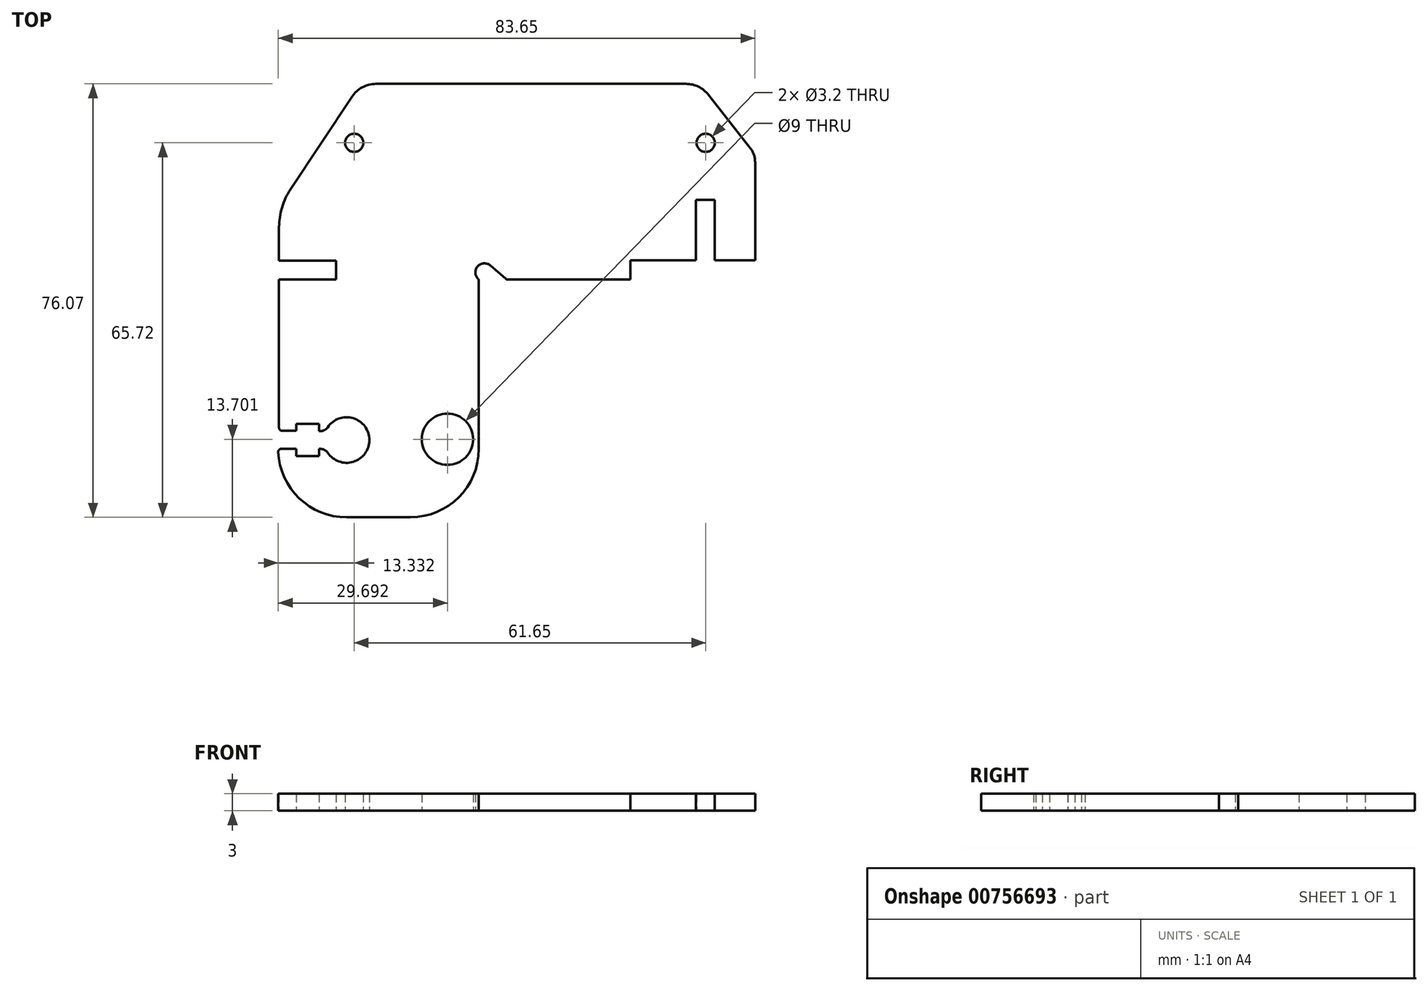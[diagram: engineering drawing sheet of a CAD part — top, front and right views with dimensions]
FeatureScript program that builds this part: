
annotation { "Feature Type Name" : "Feature", "Feature Type Description" : "" }
export const myFeature = defineFeature(function(context is Context, id is Id, definition is map)
    precondition{}
    {
        {
            var Q0;
            Q0=qCreatedBy(makeId("Top.planeOp"),FACE);
            var sketch = newSketch(context, id + "F0", { "sketchPlane" : qUnion([Q0])});
            skLineSegment(sketch, "E0", {"start": v(29.23, 6.23) * mm, "end": v(29.23, 14.01) * mm});
            skLineSegment(sketch, "E1", {"start": v(32.53, 14.01) * mm, "end": v(29.23, 14.01) * mm});
            skLineSegment(sketch, "E2", {"start": v(32.53, 14.01) * mm, "end": v(32.53, 3.36) * mm});
            skLineSegment(sketch, "E3", {"start": v(39.6, 3.36) * mm, "end": v(39.6, 22.01) * mm});
            skLineSegment(sketch, "E4", {"start": v(32.53, 3.36) * mm, "end": v(39.6, 3.36) * mm});
            skLineSegment(sketch, "E5", {"start": v(29.92, 34.35) * mm, "end": v(39.6, 22.01) * mm});
            skLineSegment(sketch, "E6", {"start": v(29.92, 34.35) * mm, "end": v(-29.62, 34.35) * mm});
            skLineSegment(sketch, "E7", {"start": v(-43.9, 12.82) * mm, "end": v(-29.62, 34.35) * mm});
            skLineSegment(sketch, "E8", {"start": v(-43.9, 12.82) * mm, "end": v(-43.9, 3.35) * mm});
            skLineSegment(sketch, "E9", {"start": v(29.23, 6.23) * mm, "end": v(29.23, 3.36) * mm});
            skLineSegment(sketch, "E10", {"start": v(29.23, 3.36) * mm, "end": v(17.7, 3.36) * mm});
            skLineSegment(sketch, "E11", {"start": v(17.7, 3.36) * mm, "end": v(17.7, 0) * mm});
            skLineSegment(sketch, "E12", {"start": v(17.7, 0) * mm, "end": v(-3.99, 0) * mm});
            skLineSegment(sketch, "E13", {"start": v(-43.9, 3.35) * mm, "end": v(-33.9, 3.35) * mm});
            skLineSegment(sketch, "E14", {"start": v(-33.9, 3.35) * mm, "end": v(-33.9, 0.05) * mm});
            skLineSegment(sketch, "E15", {"start": v(-33.9, 0.05) * mm, "end": v(-43.9, 0.05) * mm});
            skLineSegment(sketch, "E16", {"start": v(-43.9, 0.05) * mm, "end": v(-43.9, -26.52) * mm});
            skLineSegment(sketch, "E17", {"start": v(-43.9, -26.52) * mm, "end": v(-40.9, -26.52) * mm});
            skLineSegment(sketch, "E18", {"start": v(-40.9, -26.52) * mm, "end": v(-40.9, -25.32) * mm});
            skLineSegment(sketch, "E19", {"start": v(-40.9, -25.32) * mm, "end": v(-36.9, -25.32) * mm});
            skLineSegment(sketch, "E20", {"start": v(-36.9, -25.32) * mm, "end": v(-36.9, -26.59) * mm});
            skLineSegment(sketch, "E21", {"start": v(-36.9, -26.59) * mm, "end": v(-35.74, -26.59) * mm});
            skLineSegment(sketch, "E22", {"start": v(-40.9, -29.72) * mm, "end": v(-44.06, -29.72) * mm});
            skLineSegment(sketch, "E23", {"start": v(-40.9, -29.72) * mm, "end": v(-40.9, -30.99) * mm});
            skLineSegment(sketch, "E24", {"start": v(-40.9, -30.99) * mm, "end": v(-36.9, -30.99) * mm});
            skLineSegment(sketch, "E25", {"start": v(-36.9, -30.99) * mm, "end": v(-36.9, -29.72) * mm});
            skLineSegment(sketch, "E26", {"start": v(-36.9, -29.72) * mm, "end": v(-35.74, -29.72) * mm});
            skArc(sketch, "E27", {"start": v(-35.74, -29.72) * mm, "mid": v(-28.06, -28.15) * mm, "end": v(-35.74, -26.59) * mm});
            skLineSegment(sketch, "E28", {"start": v(-44.06, -29.72) * mm, "end": v(-44.06, -41.72) * mm});
            skLineSegment(sketch, "E29", {"start": v(-44.06, -41.72) * mm, "end": v(-32.06, -41.72) * mm});
            skLineSegment(sketch, "E30", {"start": v(-32.06, -41.72) * mm, "end": v(-20.86, -41.72) * mm});
            skLineSegment(sketch, "E31", {"start": v(-20.86, -41.72) * mm, "end": v(-8.86, -41.72) * mm});
            skLineSegment(sketch, "E32", {"start": v(-6.83, 2.48) * mm, "end": v(-3.99, 0) * mm});
            skArc(sketch, "E33", {"start": v(-6.83, 2.48) * mm, "mid": v(-9.1, 2.27) * mm, "end": v(-8.86, 0) * mm});
            skCircle(sketch, "E34", {"center": v(-14.36, -28.02) * mm, "radius": 4.5 * mm});
            skLineSegment(sketch, "E35", {"start": v(-8.86, 0) * mm, "end": v(-8.86, -41.72) * mm});
            skCircle(sketch, "E36", {"center": v(-30.72, 24) * mm, "radius": 1.6 * mm});
            skCircle(sketch, "E37", {"center": v(30.93, 24) * mm, "radius": 1.6 * mm});
            skSolve(sketch);
        }
        {
            var Q0;
            Q0=makeQuery(id+"F0.imprint","IMPRINT",FACE,{"disambiguationData":[TD([[makeQuery(id+"F0.imprint","IMPRINT",EDGE,{"derivedFrom":sQuery(id+"F0.wireOp",EDGE,"E0")}),1.0]])]});
            extrude(context, id + "F1", {"entities" : qUnion([Q0]), "depth" : 3 * mm, "offsetDistance" : 25 * mm});
        }
        {
            var Q0;
            Q0=makeQuery(id+"F1.opExtrude","SWEPT_EDGE",EDGE,{"disambiguationData":[OSD([sQuery(id+"F0.wireOp",EDGE,"E3"),sQuery(id+"F0.wireOp",EDGE,"E5")])]});
            fillet(context, id + "F2", {"entities" : qUnion([Q0]), "radius" : 4 * mm, "tangentPropagation" : true, "allowEdgeOverflow" : false});
        }
        {
            var Q0;
            Q0=makeQuery(id+"F1.opExtrude","SWEPT_EDGE",EDGE,{"disambiguationData":[OSD([sQuery(id+"F0.wireOp",EDGE,"E5"),sQuery(id+"F0.wireOp",EDGE,"E6")])]});
            fillet(context, id + "F3", {"entities" : qUnion([Q0]), "radius" : 5 * mm, "tangentPropagation" : true, "allowEdgeOverflow" : false});
        }
        {
            var Q0;
            Q0=makeQuery(id+"F1.opExtrude","SWEPT_EDGE",EDGE,{"disambiguationData":[OSD([sQuery(id+"F0.wireOp",EDGE,"E6"),sQuery(id+"F0.wireOp",EDGE,"E7")])]});
            fillet(context, id + "F4", {"entities" : qUnion([Q0]), "radius" : 5 * mm, "tangentPropagation" : true, "allowEdgeOverflow" : false});
        }
        {
            var Q0;
            Q0=makeQuery(id+"F1.opExtrude","SWEPT_EDGE",EDGE,{"disambiguationData":[OSD([sQuery(id+"F0.wireOp",EDGE,"E7"),sQuery(id+"F0.wireOp",EDGE,"E8")])]});
            fillet(context, id + "F5", {"entities" : qUnion([Q0]), "radius" : 12 * mm, "tangentPropagation" : true, "allowEdgeOverflow" : false});
        }
        {
            var Q0;
            Q0=makeQuery(id+"F1.opExtrude","SWEPT_EDGE",EDGE,{"disambiguationData":[OSD([sQuery(id+"F0.wireOp",EDGE,"E28"),sQuery(id+"F0.wireOp",EDGE,"E29")])]});
            var Q1;
            Q1=makeQuery(id+"F1.opExtrude","SWEPT_EDGE",EDGE,{"disambiguationData":[OSD([sQuery(id+"F0.wireOp",EDGE,"E31"),sQuery(id+"F0.wireOp",EDGE,"6QOkiaSS-hfcB-iot9-xQKw-vtsidawFotyr")])]});
            fillet(context, id + "F6", {"entities" : qUnion([Q0, Q1]), "radius" : 12 * mm, "tangentPropagation" : true, "allowEdgeOverflow" : false});
        }
        {
            var Q0;
            Q0=makeQuery(id+"F1.opExtrude","SWEPT_EDGE",EDGE,{"disambiguationData":[OSD([sQuery(id+"F0.wireOp",EDGE,"E16"),sQuery(id+"F0.wireOp",EDGE,"E17")])]});
            var Q1;
            Q1=makeQuery(id+"F6.opFillet","BLEND_EDGE",EDGE,{"blendedFrom":[makeQuery(id+"F1.opExtrude","SWEPT_EDGE",EDGE,{"disambiguationData":[OSD([sQuery(id+"F0.wireOp",EDGE,"E28"),sQuery(id+"F0.wireOp",EDGE,"E29")])]}),makeQuery(id+"F1.opExtrude","SWEPT_FACE",FACE,{"disambiguationData":[OSD([sQuery(id+"F0.wireOp",EDGE,"E22")])]})],"blendedInto":[makeQuery(id+"F1.opExtrude","SWEPT_FACE",FACE,{"disambiguationData":[OSD([sQuery(id+"F0.wireOp",EDGE,"E22")])]})]});
            fillet(context, id + "F7", {"entities" : qUnion([Q0, Q1]), "radius" : 0.5 * mm, "tangentPropagation" : true, "allowEdgeOverflow" : false});
        }
        {
            var Q0;
            Q0=makeQuery(id+"F1.opExtrude","SWEPT_EDGE",EDGE,{"disambiguationData":[OSD([sQuery(id+"F0.wireOp",EDGE,"E21"),sQuery(id+"F0.wireOp",EDGE,"E27")])]});
            var Q1;
            Q1=makeQuery(id+"F1.opExtrude","SWEPT_EDGE",EDGE,{"disambiguationData":[OSD([sQuery(id+"F0.wireOp",EDGE,"E26"),sQuery(id+"F0.wireOp",EDGE,"E27")])]});
            fillet(context, id + "F8", {"entities" : qUnion([Q0, Q1]), "radius" : 1.5 * mm, "tangentPropagation" : true, "allowEdgeOverflow" : false});
        }
        {
            var Q0;
            Q0=makeQuery(id+"F1.opExtrude","SWEPT_EDGE",EDGE,{"disambiguationData":[OSD([sQuery(id+"F0.wireOp",EDGE,"E12"),sQuery(id+"F0.wireOp",EDGE,"E32")])]});
            var Q1;
            Q1=makeQuery(id+"F1.opExtrude","SWEPT_EDGE",EDGE,{"disambiguationData":[OSD([sQuery(id+"F0.wireOp",EDGE,"E32"),sQuery(id+"F0.wireOp",EDGE,"E33")])]});
            var Q2;
            Q2=makeQuery(id+"F1.opExtrude","SWEPT_EDGE",EDGE,{"disambiguationData":[OSD([sQuery(id+"F0.wireOp",EDGE,"6QOkiaSS-hfcB-iot9-xQKw-vtsidawFotyr"),sQuery(id+"F0.wireOp",EDGE,"E33")])]});
            fillet(context, id + "F9", {"entities" : qUnion([Q0, Q1, Q2]), "radius" : 0.5 * mm, "tangentPropagation" : true, "allowEdgeOverflow" : false});
        }
        {
            var Q0;
            Q0=makeQuery(id+"F1.opExtrude","SWEPT_BODY",BODY,{"disambiguationData":[OSD([sQuery(id+"F0.wireOp",EDGE,"E0"),sQuery(id+"F0.wireOp",EDGE,"E1"),sQuery(id+"F0.wireOp",EDGE,"E2"),sQuery(id+"F0.wireOp",EDGE,"E3"),sQuery(id+"F0.wireOp",EDGE,"E4"),sQuery(id+"F0.wireOp",EDGE,"E5"),sQuery(id+"F0.wireOp",EDGE,"E6"),sQuery(id+"F0.wireOp",EDGE,"E7"),sQuery(id+"F0.wireOp",EDGE,"E8"),sQuery(id+"F0.wireOp",EDGE,"E9"),sQuery(id+"F0.wireOp",EDGE,"E10"),sQuery(id+"F0.wireOp",EDGE,"E11"),sQuery(id+"F0.wireOp",EDGE,"E12"),sQuery(id+"F0.wireOp",EDGE,"E13"),sQuery(id+"F0.wireOp",EDGE,"E14"),sQuery(id+"F0.wireOp",EDGE,"E15"),sQuery(id+"F0.wireOp",EDGE,"E16"),sQuery(id+"F0.wireOp",EDGE,"E17"),sQuery(id+"F0.wireOp",EDGE,"E18"),sQuery(id+"F0.wireOp",EDGE,"E19"),sQuery(id+"F0.wireOp",EDGE,"E20"),sQuery(id+"F0.wireOp",EDGE,"E21"),sQuery(id+"F0.wireOp",EDGE,"E22"),sQuery(id+"F0.wireOp",EDGE,"E23"),sQuery(id+"F0.wireOp",EDGE,"E24"),sQuery(id+"F0.wireOp",EDGE,"E25"),sQuery(id+"F0.wireOp",EDGE,"E26"),sQuery(id+"F0.wireOp",EDGE,"E27"),sQuery(id+"F0.wireOp",EDGE,"E28"),sQuery(id+"F0.wireOp",EDGE,"E29"),sQuery(id+"F0.wireOp",EDGE,"E30"),sQuery(id+"F0.wireOp",EDGE,"E31"),sQuery(id+"F0.wireOp",EDGE,"E32"),sQuery(id+"F0.wireOp",EDGE,"E33"),sQuery(id+"F0.wireOp",EDGE,"E34"),sQuery(id+"F0.wireOp",EDGE,"E35"),sQuery(id+"F0.wireOp",EDGE,"E36"),sQuery(id+"F0.wireOp",EDGE,"E37")])]});
            transform(context, id + "F10", {"entities" : qUnion([Q0]), "transformType" : TransformType.TRANSLATION_3D, "dx" : 0 * mm, "dy" : 0 * mm, "dz" : 0 * mm, "makeCopy" : true});
        }
        {
            var Q0;
            Q0=makeQuery(id+"F10.opPattern","COPY",BODY,{"derivedFrom":makeQuery(id+"F1.opExtrude","SWEPT_BODY",BODY,{"disambiguationData":[OSD([sQuery(id+"F0.wireOp",EDGE,"E0"),sQuery(id+"F0.wireOp",EDGE,"E1"),sQuery(id+"F0.wireOp",EDGE,"E2"),sQuery(id+"F0.wireOp",EDGE,"E3"),sQuery(id+"F0.wireOp",EDGE,"E4"),sQuery(id+"F0.wireOp",EDGE,"E5"),sQuery(id+"F0.wireOp",EDGE,"E6"),sQuery(id+"F0.wireOp",EDGE,"E7"),sQuery(id+"F0.wireOp",EDGE,"E8"),sQuery(id+"F0.wireOp",EDGE,"E9"),sQuery(id+"F0.wireOp",EDGE,"E10"),sQuery(id+"F0.wireOp",EDGE,"E11"),sQuery(id+"F0.wireOp",EDGE,"E12"),sQuery(id+"F0.wireOp",EDGE,"E13"),sQuery(id+"F0.wireOp",EDGE,"E14"),sQuery(id+"F0.wireOp",EDGE,"E15"),sQuery(id+"F0.wireOp",EDGE,"E16"),sQuery(id+"F0.wireOp",EDGE,"E17"),sQuery(id+"F0.wireOp",EDGE,"E18"),sQuery(id+"F0.wireOp",EDGE,"E19"),sQuery(id+"F0.wireOp",EDGE,"E20"),sQuery(id+"F0.wireOp",EDGE,"E21"),sQuery(id+"F0.wireOp",EDGE,"E22"),sQuery(id+"F0.wireOp",EDGE,"E23"),sQuery(id+"F0.wireOp",EDGE,"E24"),sQuery(id+"F0.wireOp",EDGE,"E25"),sQuery(id+"F0.wireOp",EDGE,"E26"),sQuery(id+"F0.wireOp",EDGE,"E27"),sQuery(id+"F0.wireOp",EDGE,"E28"),sQuery(id+"F0.wireOp",EDGE,"E29"),sQuery(id+"F0.wireOp",EDGE,"E30"),sQuery(id+"F0.wireOp",EDGE,"E31"),sQuery(id+"F0.wireOp",EDGE,"E32"),sQuery(id+"F0.wireOp",EDGE,"E33"),sQuery(id+"F0.wireOp",EDGE,"E34"),sQuery(id+"F0.wireOp",EDGE,"E35"),sQuery(id+"F0.wireOp",EDGE,"E36"),sQuery(id+"F0.wireOp",EDGE,"E37")])]}),"instanceName":"1"});
            deleteBodies(context, id + "F11", {"entities" : qUnion([Q0])});
        }
    });
